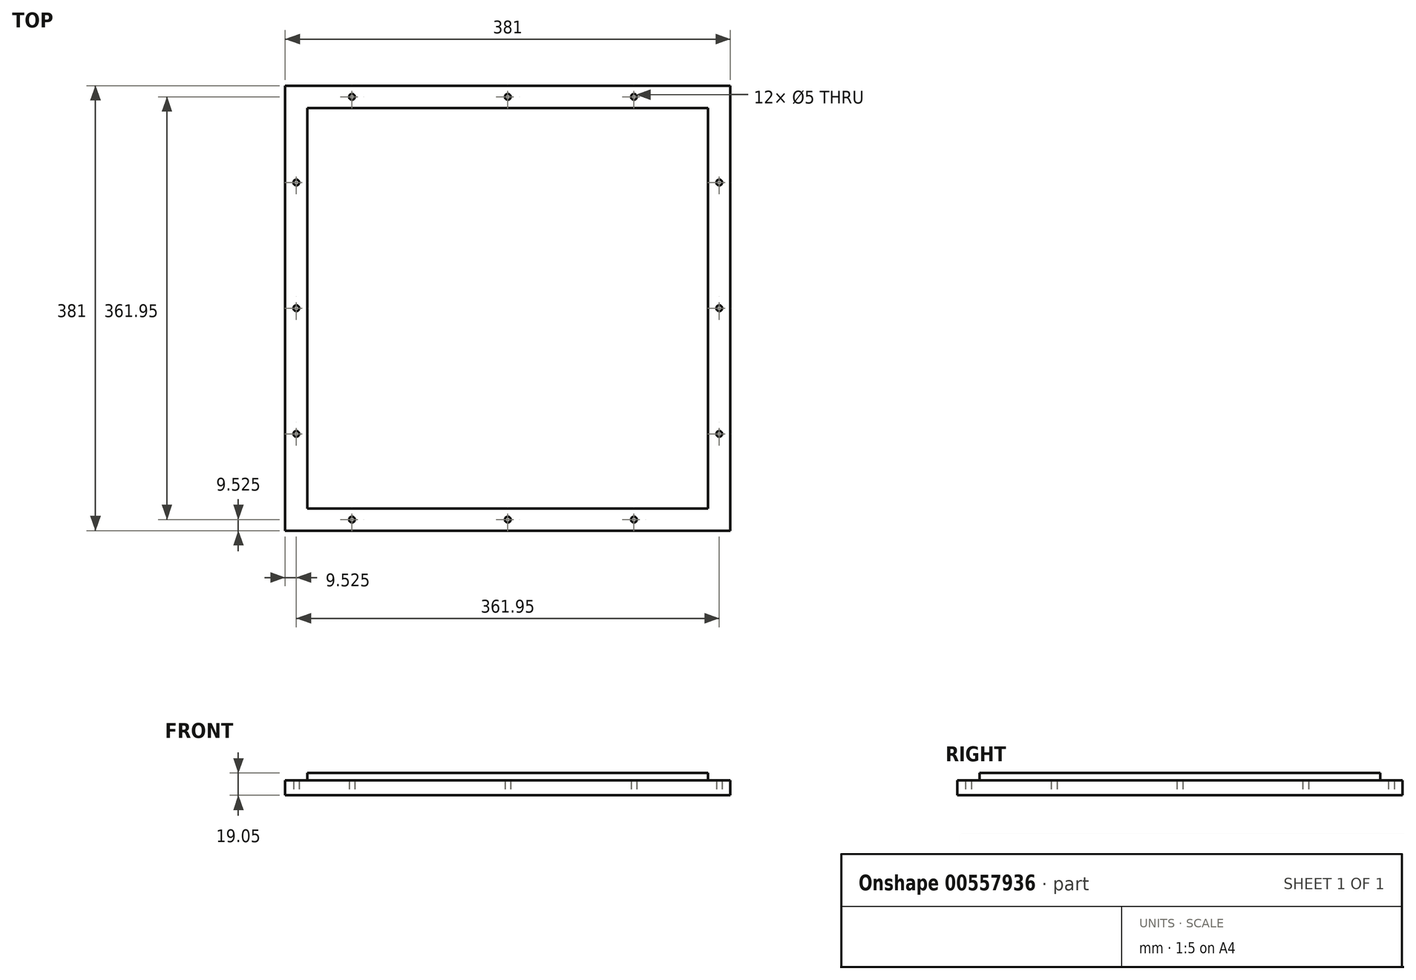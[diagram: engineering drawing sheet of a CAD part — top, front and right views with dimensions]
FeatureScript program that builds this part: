
annotation { "Feature Type Name" : "Feature", "Feature Type Description" : "" }
export const myFeature = defineFeature(function(context is Context, id is Id, definition is map)
    precondition{}
    {
        {
            var Q0;
            Q0=qCreatedBy(makeId("Top.planeOp"),FACE);
            var sketch = newSketch(context, id + "F0", { "sketchPlane" : qUnion([Q0])});
            skLineSegment(sketch, "E0.bottom", {"start": v(30.48, 17.78) * mm, "end": v(411.48, 17.78) * mm});
            skLineSegment(sketch, "E0.top", {"start": v(30.48, 398.78) * mm, "end": v(411.48, 398.78) * mm});
            skLineSegment(sketch, "E0.left", {"start": v(30.48, 17.78) * mm, "end": v(30.48, 398.78) * mm});
            skLineSegment(sketch, "E0.right", {"start": v(411.48, 17.78) * mm, "end": v(411.48, 398.78) * mm});
            skPoint(sketch, "E0.middle", {"position": v(220.98, 208.28) * mm});
            skLineSegment(sketch, "E1.bottom", {"start": v(392.43, 379.73) * mm, "end": v(49.53, 379.73) * mm});
            skLineSegment(sketch, "E1.top", {"start": v(392.43, 36.83) * mm, "end": v(49.53, 36.83) * mm});
            skLineSegment(sketch, "E1.left", {"start": v(392.43, 379.73) * mm, "end": v(392.43, 36.83) * mm});
            skLineSegment(sketch, "E1.right", {"start": v(49.53, 379.73) * mm, "end": v(49.53, 36.83) * mm});
            skCircle(sketch, "E2", {"center": v(220.98, 389.26) * mm, "radius": 2.5 * mm});
            skPoint(sketch, "E3.endSnap0", {"position": v(30.48, 208.28) * mm});
            skCircle(sketch, "E4.MirrorC", {"center": v(40, 208.28) * mm, "radius": 2.5 * mm});
            skCircle(sketch, "E5.MirrorC", {"center": v(40, 315.9) * mm, "radius": 2.5 * mm});
            skCircle(sketch, "E6.MirrorC", {"center": v(87.63, 389.25) * mm, "radius": 2.5 * mm});
            skCircle(sketch, "E7.MirrorC", {"center": v(220.98, 27.3) * mm, "radius": 2.5 * mm});
            skCircle(sketch, "E8.MirrorC", {"center": v(87.63, 27.3) * mm, "radius": 2.5 * mm});
            skCircle(sketch, "E9.MirrorC", {"center": v(40, 100.67) * mm, "radius": 2.5 * mm});
            skCircle(sketch, "E10.MirrorC", {"center": v(328.93, 389.25) * mm, "radius": 2.5 * mm});
            skCircle(sketch, "E11.MirrorC", {"center": v(401.96, 315.9) * mm, "radius": 2.5 * mm});
            skCircle(sketch, "E12.MirrorC", {"center": v(401.96, 208.28) * mm, "radius": 2.5 * mm});
            skCircle(sketch, "E13.MirrorC", {"center": v(401.96, 100.67) * mm, "radius": 2.5 * mm});
            skCircle(sketch, "E14.MirrorC", {"center": v(328.93, 27.3) * mm, "radius": 2.5 * mm});
            skSolve(sketch);
        }
        {
            var Q0;
            Q0=makeQuery(id+"F0.imprint","IMPRINT",FACE,{"disambiguationData":[TD([[makeQuery(id+"F0.imprint","IMPRINT",EDGE,{"derivedFrom":sQuery(id+"F0.wireOp",EDGE,"E0.bottom")}),1.0]])]});
            extrude(context, id + "F1", {"entities" : qUnion([Q0]), "depth" : 12.7 * mm, "offsetDistance" : 25.4 * mm});
        }
        {
            var Q0;
            Q0=makeQuery(id+"F0.imprint","IMPRINT",FACE,{"disambiguationData":[TD([[makeQuery(id+"F0.imprint","IMPRINT",EDGE,{"derivedFrom":sQuery(id+"F0.wireOp",EDGE,"E1.bottom")}),1.0]])]});
            extrude(context, id + "F2", {"entities" : qUnion([Q0]), "operationType" : NewBodyOperationType.ADD, "depth" : 19.05 * mm, "offsetDistance" : 25.4 * mm});
        }
    });
